# Revit family: Santa_Fe_Advance_90_Dehumidifiers
name_source: partatom
category: Mechanical Equipment
revit_build: Autodesk Revit 2016 (Build: 20150714_1515(x64)
units: mm (PartAtom-declared; Revit-internal decimal feet)

## family parameters
Always vertical = Yes
Cut with Voids When Loaded = No
OmniClass Number = 23.75.00.00
OmniClass Title = Climate Control (HVAC)
Part Type = Normal
Room Calculation Point = No
Round Connector Dimension = Use Diameter
Shared = No
Work Plane-Based = No

## types (1)
- Santa_Fe_Advance_90_Dehumidifiers
    Basement Sizing = 2,200-2,600 Sq. Ft. / 22,000-26,000 Cu. Ft.
    Blower = 309 CFM @ 0.0” WG
    Crawl Space Sizing = 2,200-3,000 Sq. Ft. / 11,000-15,000 Cu. Ft.
    Current Draw = 5.7 amps
    Drain Connection = 3/4” Threaded Female NPT
    Drain Hose = 8’ Direct Gravity Drain Hose (5/8” ID x 7/8” OD)
    Efficiency = 6.1 Pints/kWh	 4.9 Pints/kWh
    Energy Factor = 2.88 L/kWh	 2.3 L/kWh
    Operating Temperature = 49°F Min., 95°F Max.
    Pallet Quantity = 4 per pallet
    Power = 640 watts @ 80°F and 60% RH
    Power Cord = 9’, 115 VAC, Ground   
Plug Type B
(USA, MEX, CAN, JPN)
    Refrigerant = R410A, 15 oz.
    Shipping Dimensions = 23”W x 30”H x 40”D
    Shipping Options = UPS and LTL
    Shipping Weight = 95 lbs.
    Supply Voltage = 115 volt – 1 phase – 60 Hz
    Trap = Yes
    UPC Number = 859029004939
    URL = www.santa-fe-products.com/dehumidifiers/advance-90/
    Unit Dimensions = 14.5”W x 19.4”H x 26”D
    Unit Weight = 80 lbs.
    Water Removal = @ 80°F and 60%RH    @ 70°F and 60%RH
90 Pints / 11.25 Gallons     71 Pints / 8.875 Gallons
    Wireframe = Yes

## geometry (parser evidence)
native form markers: Sweep x12
no freeform markers — native parametric forms only
